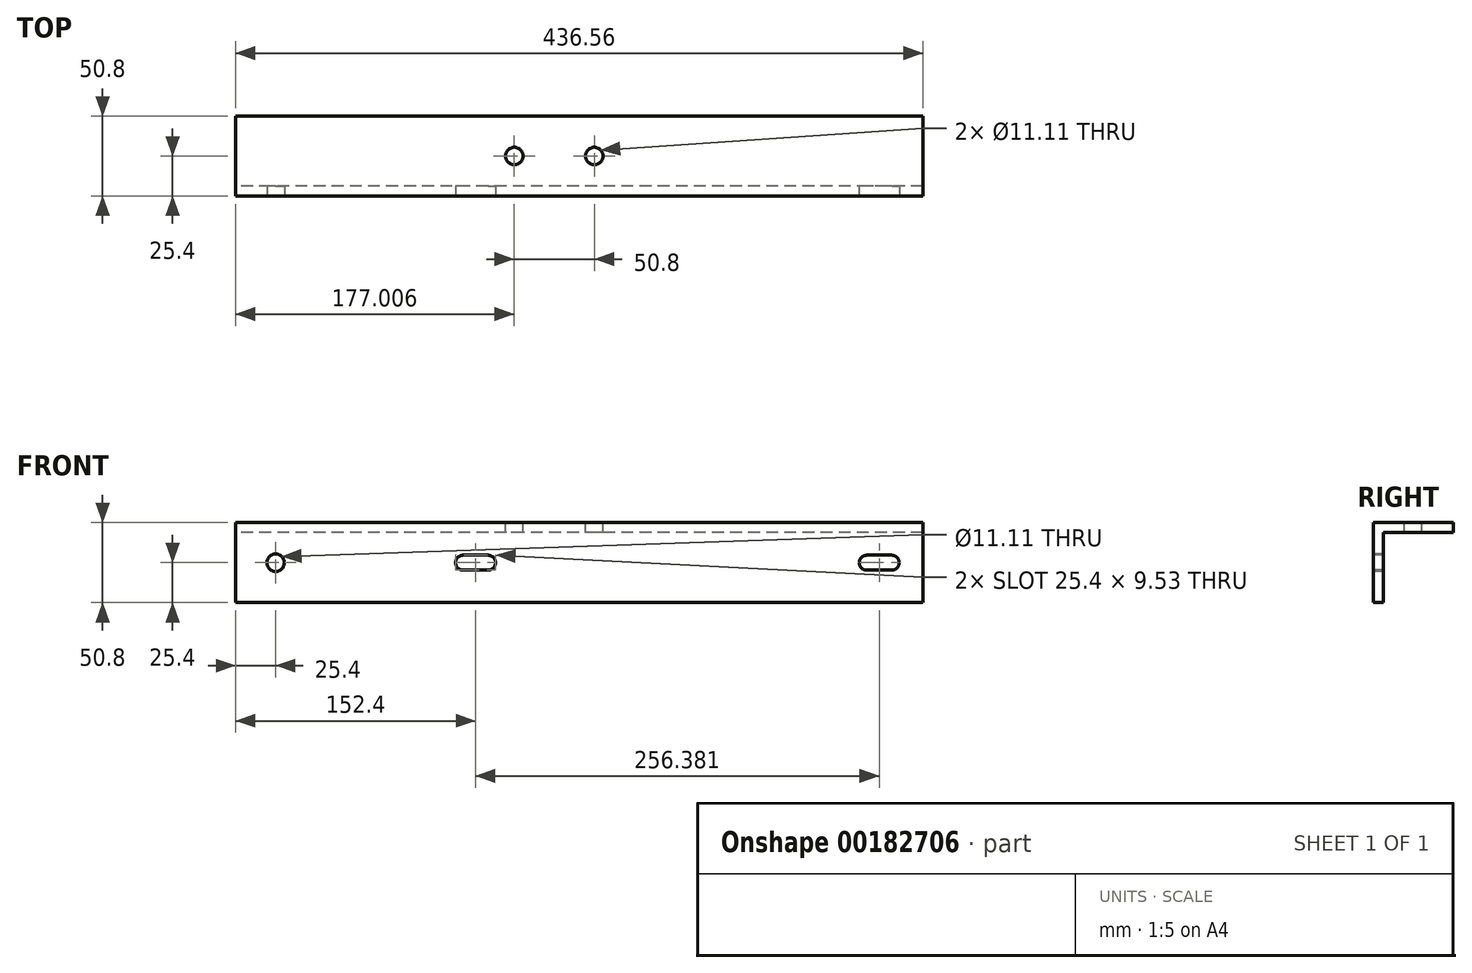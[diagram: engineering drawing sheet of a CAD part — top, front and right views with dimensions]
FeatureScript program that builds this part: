
annotation { "Feature Type Name" : "Feature", "Feature Type Description" : "" }
export const myFeature = defineFeature(function(context is Context, id is Id, definition is map)
    precondition{}
    {
        {
            var Q0;
            Q0=qCreatedBy(makeId("Right.planeOp"),FACE);
            var sketch = newSketch(context, id + "F0", { "sketchPlane" : qUnion([Q0])});
            skLineSegment(sketch, "E0", {"start": v(0, 0) * mm, "end": v(0, 50.8) * mm});
            skLineSegment(sketch, "E1", {"start": v(0, 50.8) * mm, "end": v(6.35, 50.8) * mm});
            skLineSegment(sketch, "E2", {"start": v(6.35, 50.8) * mm, "end": v(6.35, 6.35) * mm});
            skLineSegment(sketch, "E3", {"start": v(6.35, 6.35) * mm, "end": v(50.8, 6.35) * mm});
            skLineSegment(sketch, "E4", {"start": v(50.8, 6.35) * mm, "end": v(50.8, 0) * mm});
            skLineSegment(sketch, "E5", {"start": v(50.8, 0) * mm, "end": v(0, 0) * mm});
            skSolve(sketch);
        }
        {
            var Q0;
            Q0=makeQuery(id+"F0.imprint","IMPRINT",FACE,{"disambiguationData":[TD([[makeQuery(id+"F0.imprint","IMPRINT",EDGE,{"derivedFrom":sQuery(id+"F0.wireOp",EDGE,"E0")}),-1.0]])]});
            extrude(context, id + "F1", {"entities" : qUnion([Q0]), "depth" : 436.56 * mm});
        }
        {
            var Q0;
            Q0=makeQuery(id+"F1.opExtrude","SWEPT_FACE",FACE,{"disambiguationData":[OSD([sQuery(id+"F0.wireOp",EDGE,"E0")])]});
            var sketch = newSketch(context, id + "F2", { "sketchPlane" : qUnion([Q0])});
            skCircle(sketch, "E6", {"center": v(25.4, 25.4) * mm, "radius": 5.56 * mm});
            skLineSegment(sketch, "E7", {"start": v(144.46, 25.4) * mm, "end": v(160.34, 25.4) * mm});
            skArc(sketch, "E8.0.startCap", {"start": v(144.46, 20.64) * mm, "mid": v(139.7, 25.4) * mm, "end": v(144.46, 30.16) * mm});
            skArc(sketch, "E8.0.endCap", {"start": v(160.34, 30.16) * mm, "mid": v(165.1, 25.4) * mm, "end": v(160.34, 20.64) * mm});
            skLineSegment(sketch, "E8.0.left", {"start": v(144.46, 30.16) * mm, "end": v(160.34, 30.16) * mm});
            skLineSegment(sketch, "E8.0.right", {"start": v(144.46, 20.64) * mm, "end": v(160.34, 20.64) * mm});
            skLineSegment(sketch, "E9", {"start": v(400.84, 25.4) * mm, "end": v(416.72, 25.4) * mm});
            skArc(sketch, "E10.0.startCap", {"start": v(400.84, 20.64) * mm, "mid": v(396.08, 25.4) * mm, "end": v(400.84, 30.16) * mm});
            skArc(sketch, "E10.0.endCap", {"start": v(416.72, 30.16) * mm, "mid": v(421.48, 25.4) * mm, "end": v(416.72, 20.64) * mm});
            skLineSegment(sketch, "E10.0.left", {"start": v(400.84, 30.16) * mm, "end": v(416.72, 30.16) * mm});
            skLineSegment(sketch, "E10.0.right", {"start": v(400.84, 20.64) * mm, "end": v(416.72, 20.64) * mm});
            skSolve(sketch);
        }
        {
            var Q0;
            Q0=qSketchRegion(id+"F2",true);
            extrude(context, id + "F3", {"entities" : qUnion([Q0]), "operationType" : NewBodyOperationType.REMOVE, "endBound" : BoundingType.THROUGH_ALL, "oppositeDirection" : true, "depth" : 25.4 * mm});
        }
        {
            var Q0;
            Q0=makeQuery(id+"F1.opExtrude","SWEPT_FACE",FACE,{"disambiguationData":[OSD([sQuery(id+"F0.wireOp",EDGE,"E5")])]});
            var sketch = newSketch(context, id + "F4", { "sketchPlane" : qUnion([Q0])});
            skCircle(sketch, "E11", {"center": v(177, -25.4) * mm, "radius": 5.56 * mm});
            skCircle(sketch, "E12", {"center": v(227.8, -25.4) * mm, "radius": 5.56 * mm});
            skSolve(sketch);
        }
        {
            var Q0;
            Q0=makeQuery(id+"F4.imprint","IMPRINT",FACE,{"disambiguationData":[TD([[makeQuery(id+"F4.imprint","IMPRINT",EDGE,{"derivedFrom":sQuery(id+"F4.wireOp",EDGE,"E12")}),1.0]])]});
            var Q1;
            Q1=makeQuery(id+"F4.imprint","IMPRINT",FACE,{"disambiguationData":[TD([[makeQuery(id+"F4.imprint","IMPRINT",EDGE,{"derivedFrom":sQuery(id+"F4.wireOp",EDGE,"E11")}),1.0]])]});
            extrude(context, id + "F5", {"entities" : qUnion([Q0, Q1]), "operationType" : NewBodyOperationType.REMOVE, "endBound" : BoundingType.THROUGH_ALL, "oppositeDirection" : true, "depth" : 25.4 * mm});
        }
        {
            var Q0;
            Q0=makeQuery(id+"F1.opExtrude","SWEPT_BODY",BODY,{"disambiguationData":[OSD([sQuery(id+"F0.wireOp",EDGE,"E0"),sQuery(id+"F0.wireOp",EDGE,"E1"),sQuery(id+"F0.wireOp",EDGE,"E2"),sQuery(id+"F0.wireOp",EDGE,"E3"),sQuery(id+"F0.wireOp",EDGE,"E4"),sQuery(id+"F0.wireOp",EDGE,"E5")])]});
            var Q1;
            Q1=qCreatedBy(makeId("Top.planeOp"),FACE);
            mirror(context, id + "F6", {"entities" : qUnion([Q0]), "mirrorPlane" : qUnion([Q1])});
        }
        {
            var Q0;
            Q0=makeQuery(id+"F1.opExtrude","SWEPT_BODY",BODY,{"disambiguationData":[OSD([sQuery(id+"F0.wireOp",EDGE,"E0"),sQuery(id+"F0.wireOp",EDGE,"E1"),sQuery(id+"F0.wireOp",EDGE,"E2"),sQuery(id+"F0.wireOp",EDGE,"E3"),sQuery(id+"F0.wireOp",EDGE,"E4"),sQuery(id+"F0.wireOp",EDGE,"E5")])]});
            deleteBodies(context, id + "F7", {"entities" : qUnion([Q0])});
        }
    });
